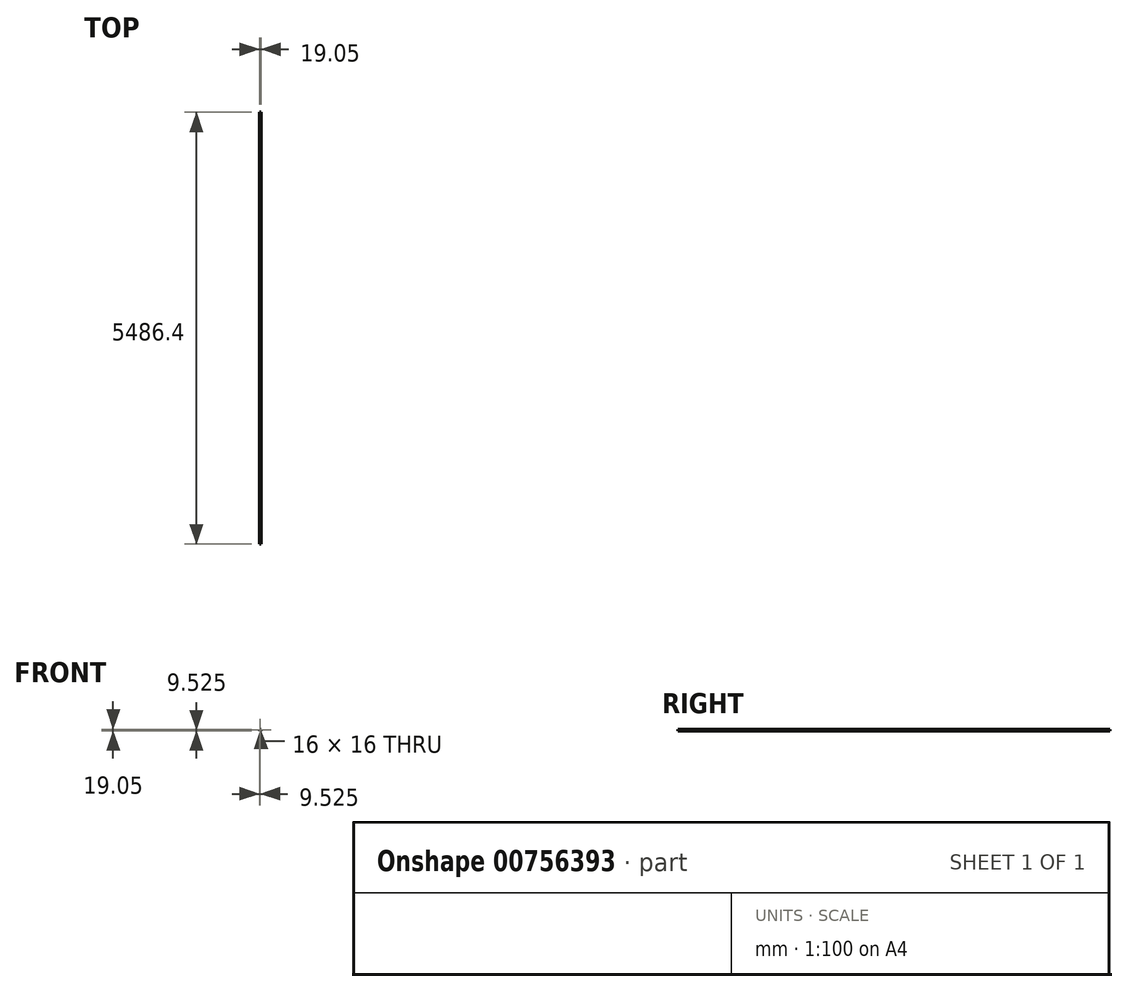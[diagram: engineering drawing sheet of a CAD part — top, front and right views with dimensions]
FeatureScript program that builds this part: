
annotation { "Feature Type Name" : "Feature", "Feature Type Description" : "" }
export const myFeature = defineFeature(function(context is Context, id is Id, definition is map)
    precondition{}
    {
        {
            var Q0;
            Q0=qCreatedBy(makeId("Front.planeOp"),FACE);
            var sketch = newSketch(context, id + "F0", { "sketchPlane" : qUnion([Q0])});
            skLineSegment(sketch, "E0.bottom", {"start": v(1.52, 17.53) * mm, "end": v(17.53, 17.53) * mm});
            skLineSegment(sketch, "E0.top", {"start": v(1.52, 1.52) * mm, "end": v(17.53, 1.52) * mm});
            skLineSegment(sketch, "E0.left", {"start": v(1.52, 17.53) * mm, "end": v(1.52, 1.52) * mm});
            skLineSegment(sketch, "E0.right", {"start": v(17.53, 17.53) * mm, "end": v(17.53, 1.52) * mm});
            skLineSegment(sketch, "E1.bottom", {"start": v(0, 0) * mm, "end": v(19.05, 0) * mm});
            skLineSegment(sketch, "E1.top", {"start": v(0, 19.05) * mm, "end": v(19.05, 19.05) * mm});
            skLineSegment(sketch, "E1.left", {"start": v(0, 0) * mm, "end": v(0, 19.05) * mm});
            skLineSegment(sketch, "E1.right", {"start": v(19.05, 0) * mm, "end": v(19.05, 19.05) * mm});
            skSolve(sketch);
        }
        {
            var Q0;
            Q0=makeQuery(id+"F0.imprint","IMPRINT",FACE,{"disambiguationData":[TD([[makeQuery(id+"F0.imprint","IMPRINT",EDGE,{"derivedFrom":sQuery(id+"F0.wireOp",EDGE,"E0.bottom")}),1.0]])]});
            extrude(context, id + "F1", {"entities" : qUnion([Q0]), "depth" : 5486.4 * mm, "offsetDistance" : 25.4 * mm});
        }
    });
